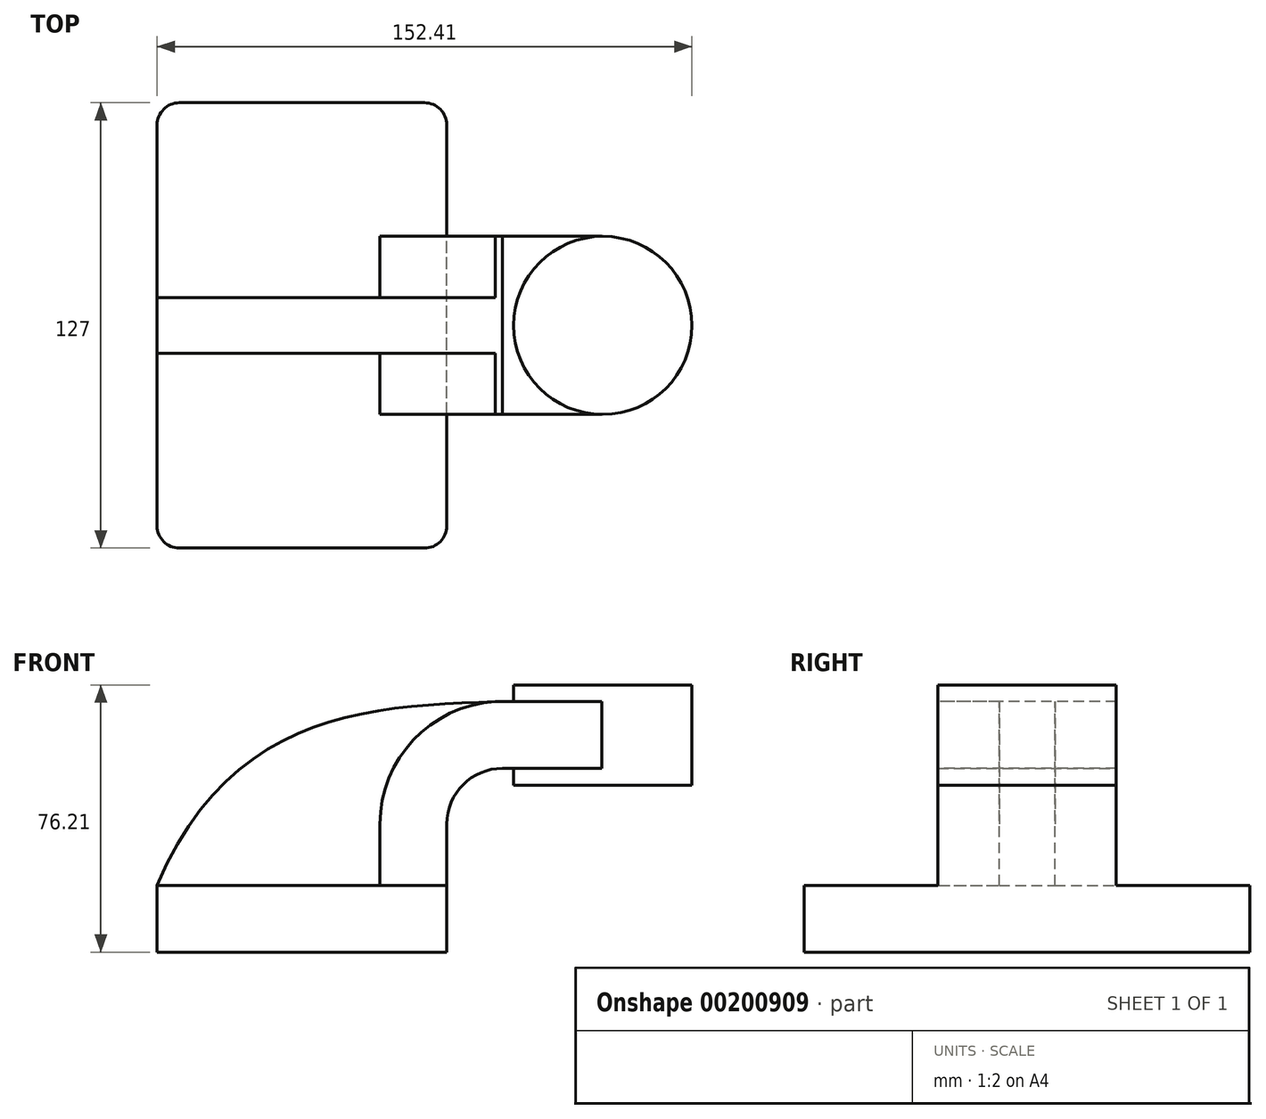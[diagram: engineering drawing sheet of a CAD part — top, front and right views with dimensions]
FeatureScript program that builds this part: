
annotation { "Feature Type Name" : "Feature", "Feature Type Description" : "" }
export const myFeature = defineFeature(function(context is Context, id is Id, definition is map)
    precondition{}
    {
        {
            var Q0;
            Q0=qCreatedBy(makeId("Front.planeOp"),FACE);
            var sketch = newSketch(context, id + "F0", { "sketchPlane" : qUnion([Q0])});
            skLineSegment(sketch, "E0.bottom", {"start": v(-41.28, 9.52) * mm, "end": v(41.27, 9.53) * mm});
            skLineSegment(sketch, "E0.top", {"start": v(-41.28, -9.53) * mm, "end": v(41.28, -9.53) * mm});
            skLineSegment(sketch, "E0.left", {"start": v(-41.28, 9.52) * mm, "end": v(-41.27, -9.53) * mm});
            skLineSegment(sketch, "E0.right", {"start": v(41.28, 9.53) * mm, "end": v(41.28, -9.52) * mm});
            skPoint(sketch, "E0.middle", {"position": v(0, 0) * mm});
            skLineSegment(sketch, "E1.bottom", {"start": v(111.12, 38.1) * mm, "end": v(60.32, 38.1) * mm});
            skLineSegment(sketch, "E1.top", {"start": v(111.12, 66.68) * mm, "end": v(60.32, 66.68) * mm});
            skLineSegment(sketch, "E1.left", {"start": v(111.12, 38.1) * mm, "end": v(111.12, 66.67) * mm});
            skLineSegment(sketch, "E1.right", {"start": v(60.32, 38.1) * mm, "end": v(60.32, 66.68) * mm});
            skPoint(sketch, "E1.middle", {"position": v(85.72, 52.39) * mm});
            skLineSegment(sketch, "E2", {"start": v(41.27, 9.53) * mm, "end": v(41.27, 27) * mm});
            skArc(sketch, "E3", {"start": v(41.27, 27) * mm, "mid": v(45.92, 38.23) * mm, "end": v(57.15, 42.88) * mm});
            skLineSegment(sketch, "E4", {"start": v(57.15, 42.88) * mm, "end": v(85.5, 42.88) * mm});
            skLineSegment(sketch, "E5.0", {"start": v(57.15, 61.93) * mm, "end": v(85.5, 61.93) * mm});
            skArc(sketch, "E5.1", {"start": v(22.23, 27) * mm, "mid": v(32.45, 51.7) * mm, "end": v(57.15, 61.93) * mm});
            skLineSegment(sketch, "E5.2", {"start": v(22.22, 9.53) * mm, "end": v(22.22, 27) * mm});
            skLineSegment(sketch, "E6", {"start": v(85.5, 42.88) * mm, "end": v(85.5, 61.93) * mm});
            skFitSpline(sketch, "E7", {"points": [v(-41.28, 9.52) * mm, v(57.15, 61.93) * mm], "startDerivative": vector(62.49, 149.58) * mm, "endDerivative": vector(110.55, 3.2) * mm});
            skLineSegment(sketch, "E8", {"start": v(60.32, 61.93) * mm, "end": v(60.32, 66.68) * mm});
            skLineSegment(sketch, "E9", {"start": v(85.72, 52.39) * mm, "end": v(85.72, 66.68) * mm});
            skLineSegment(sketch, "E10", {"start": v(85.72, 52.39) * mm, "end": v(85.72, 38.1) * mm});
            skSolve(sketch);
        }
        {
            var Q0;
            Q0=makeQuery(id+"F0.imprint","IMPRINT",FACE,{"disambiguationData":[TD([[makeQuery(id+"F0.imprint","IMPRINT",EDGE,{"derivedFrom":sQuery(id+"F0.wireOp",EDGE,"E0.top")}),1.0]])]});
            extrude(context, id + "F1", {"entities" : qUnion([Q0]), "endBound" : BoundingType.SYMMETRIC, "depth" : 127 * mm});
        }
        {
            var Q0;
            {var subQ1=sQuery(id+"F0.wireOp",EDGE,"E2");Q0=makeQuery(id+"F0.imprint","IMPRINT",FACE,{"disambiguationData":[TD([[makeQuery(id+"F0.imprint","IMPRINT",EDGE,{"derivedFrom":subQ1}),1.0]])]});}
            var Q1;
            {var subQ3=sQuery(id+"F0.wireOp",EDGE,"E6");var subQ5=sQuery(id+"F0.wireOp",EDGE,"E4");var subQ6=makeQuery(id+"F0.imprint","INTERSECT",VERTEX,{"derivedFrom":[subQ5,subQ3]});Q1=makeQuery(id+"F0.imprint","IMPRINT",FACE,{"disambiguationData":[TD([[makeQuery(id+"F0.imprint","IMPRINT",EDGE,{"disambiguationData":[TD([[subQ6,1.0]])],"derivedFrom":subQ5}),1.0]])]});}
            extrude(context, id + "F2", {"entities" : qUnion([Q0, Q1]), "operationType" : NewBodyOperationType.ADD, "endBound" : BoundingType.SYMMETRIC, "depth" : 50.8 * mm});
        }
        {
            var Q0;
            {var subQ3=sQuery(id+"F0.wireOp",EDGE,"E5.2");Q0=makeQuery(id+"F0.imprint","IMPRINT",FACE,{"disambiguationData":[TD([[makeQuery(id+"F0.imprint","IMPRINT",EDGE,{"derivedFrom":subQ3}),1.0]])]});}
            extrude(context, id + "F3", {"entities" : qUnion([Q0]), "operationType" : NewBodyOperationType.ADD, "endBound" : BoundingType.SYMMETRIC, "depth" : 15.88 * mm});
        }
        {
            var Q0;
            {var subQ1=sQuery(id+"F0.wireOp",EDGE,"E1.left");Q0=makeQuery(id+"F0.imprint","IMPRINT",FACE,{"disambiguationData":[TD([[makeQuery(id+"F0.imprint","IMPRINT",EDGE,{"derivedFrom":subQ1}),1.0]])]});}
            var Q1;
            Q1=sQuery(id+"F0.wireOp",EDGE,"E10");
            revolve(context, id + "F4", {"operationType" : NewBodyOperationType.ADD, "entities" : qUnion([Q0]), "axis" : qUnion([Q1]), "revolveType" : RevolveType.FULL});
        }
        {
            var Q0;
            Q0=makeQuery(id+"F1.opExtrude","CAP_EDGE",EDGE,{"disambiguationData":[OSD([sQuery(id+"F0.wireOp",EDGE,"E0.right")])],"isStart":false});
            var Q1;
            Q1=makeQuery(id+"F1.opExtrude","CAP_EDGE",EDGE,{"disambiguationData":[OSD([sQuery(id+"F0.wireOp",EDGE,"E0.left")])],"isStart":false});
            var Q2;
            Q2=makeQuery(id+"F1.opExtrude","CAP_EDGE",EDGE,{"disambiguationData":[OSD([sQuery(id+"F0.wireOp",EDGE,"E0.right")])],"isStart":true});
            var Q3;
            Q3=makeQuery(id+"F1.opExtrude","CAP_EDGE",EDGE,{"disambiguationData":[OSD([sQuery(id+"F0.wireOp",EDGE,"E0.left")])],"isStart":true});
            fillet(context, id + "F5", {"entities" : qUnion([Q0, Q1, Q2, Q3]), "radius" : 6.35 * mm, "tangentPropagation" : true, "allowEdgeOverflow" : false});
        }
    });
